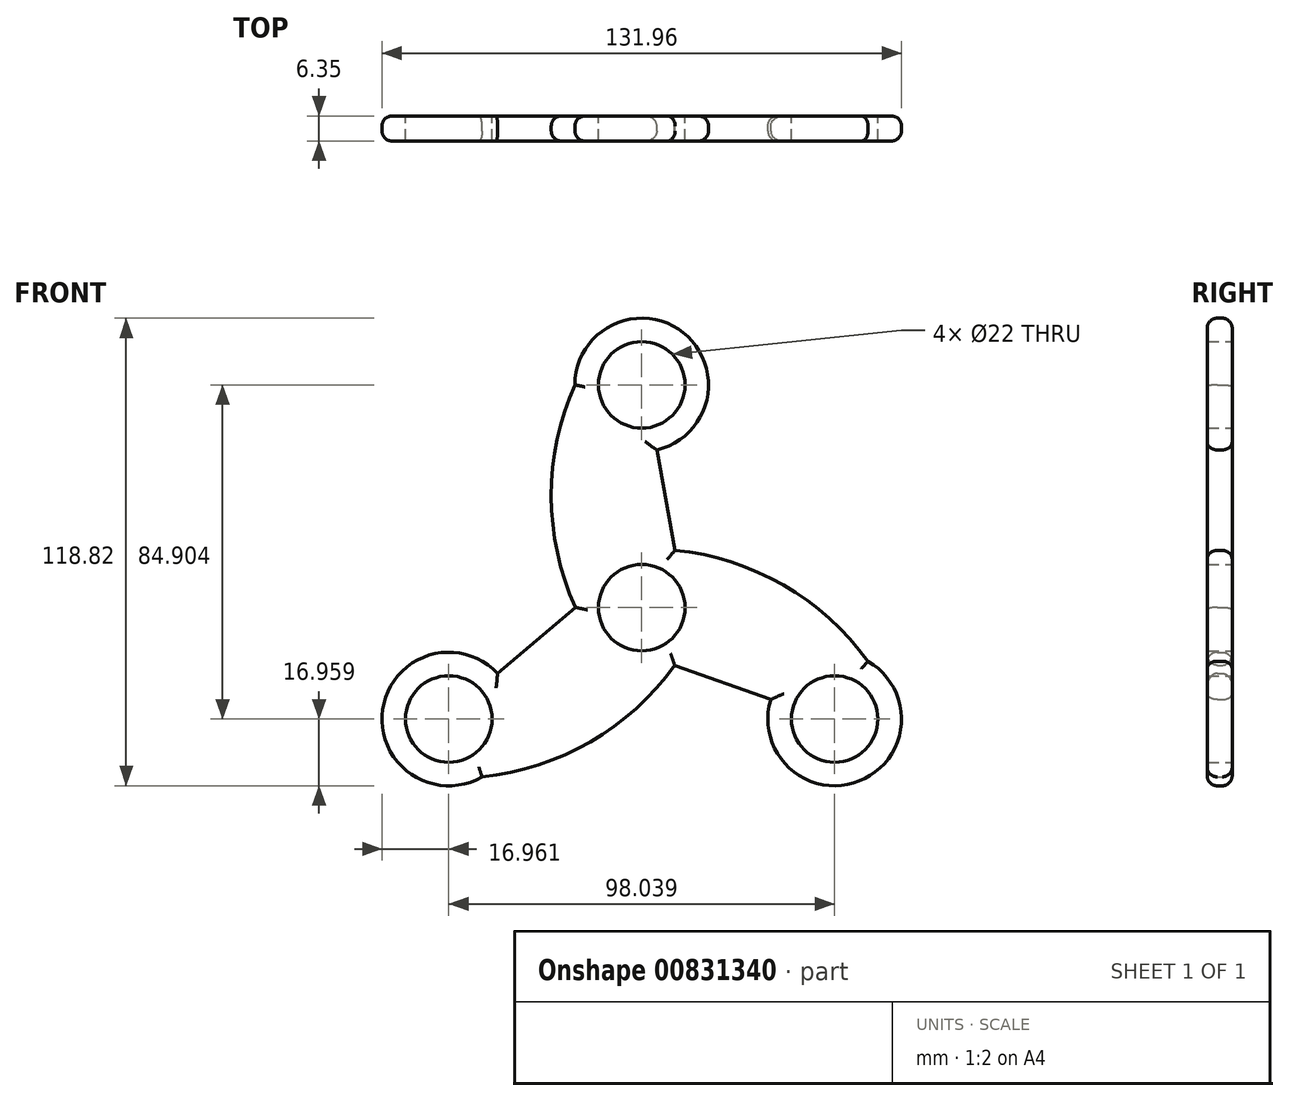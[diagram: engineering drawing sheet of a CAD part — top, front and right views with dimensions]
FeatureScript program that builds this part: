
annotation { "Feature Type Name" : "Feature", "Feature Type Description" : "" }
export const myFeature = defineFeature(function(context is Context, id is Id, definition is map)
    precondition{}
    {
        {
            var Q0;
            Q0=qCreatedBy(makeId("Front.planeOp"),FACE);
            var sketch = newSketch(context, id + "F0", { "sketchPlane" : qUnion([Q0])});
            skCircle(sketch, "E0", {"center": v(0, 0) * mm, "radius": 11 * mm});
            skCircle(sketch, "E1", {"center": v(0, 56.6) * mm, "radius": 11 * mm});
            skArc(sketch, "E2", {"start": v(3.84, 40.08) * mm, "mid": v(10.55, 69.89) * mm, "end": v(-16.96, 56.6) * mm});
            skArc(sketch, "E3", {"start": v(-16.82, 0.13) * mm, "mid": v(-16.82, 0.07) * mm, "end": v(-16.83, 0) * mm});
            skArc(sketch, "E4", {"start": v(-16.96, 56.6) * mm, "mid": v(-22.98, 28.29) * mm, "end": v(-16.83, 0) * mm});
            skLineSegment(sketch, "E5", {"start": v(3.84, 40.08) * mm, "end": v(8.53, 14.5) * mm});
            skCircle(sketch, "E6.1.0", {"center": v(-49.02, -28.3) * mm, "radius": 11 * mm});
            skArc(sketch, "E6.1.1", {"start": v(-36.64, -16.71) * mm, "mid": v(-65.8, -25.8) * mm, "end": v(-40.54, -42.99) * mm});
            skLineSegment(sketch, "E6.1.2", {"start": v(-36.64, -16.71) * mm, "end": v(-16.82, 0.13) * mm});
            skArc(sketch, "E6.1.3", {"start": v(-40.54, -42.99) * mm, "mid": v(-13, -34.04) * mm, "end": v(8.41, -14.57) * mm});
            skCircle(sketch, "E6.2.0", {"center": v(49.02, -28.3) * mm, "radius": 11 * mm});
            skArc(sketch, "E6.2.1", {"start": v(32.8, -23.37) * mm, "mid": v(55.25, -44.08) * mm, "end": v(57.5, -13.61) * mm});
            skLineSegment(sketch, "E6.2.2", {"start": v(32.8, -23.37) * mm, "end": v(8.3, -14.64) * mm});
            skArc(sketch, "E6.2.3", {"start": v(57.5, -13.61) * mm, "mid": v(35.99, 5.76) * mm, "end": v(8.41, 14.57) * mm});
            skArc(sketch, "E7.trimOffspring", {"start": v(8.53, 14.5) * mm, "mid": v(8.47, 14.54) * mm, "end": v(8.41, 14.57) * mm});
            skArc(sketch, "E8.trimOffspring", {"start": v(8.3, -14.64) * mm, "mid": v(8.36, -14.6) * mm, "end": v(8.41, -14.57) * mm});
            skSolve(sketch);
        }
        {
            var Q0;
            Q0 = qSketchRegion(id + "F0", true);
            extrude(context, id + "F1", {"entities" : qUnion([Q0]), "depth" : 6.35 * mm, "offsetDistance" : 25.4 * mm});
        }
        {
            var Q0;
            Q0=makeQuery(id+"F1.opExtrude","CAP_EDGE",EDGE,{"disambiguationData":[OSD([sQuery(id+"F0.wireOp",EDGE,"E2")])],"isStart":false});
            var Q1;
            Q1=makeQuery(id+"F1.opExtrude","CAP_EDGE",EDGE,{"disambiguationData":[OSD([sQuery(id+"F0.wireOp",EDGE,"E5")])],"isStart":false});
            var Q2;
            Q2=makeQuery(id+"F1.opExtrude","CAP_EDGE",EDGE,{"disambiguationData":[OSD([sQuery(id+"F0.wireOp",EDGE,"E4")])],"isStart":false});
            var Q3;
            Q3=makeQuery(id+"F1.opExtrude","CAP_EDGE",EDGE,{"disambiguationData":[OSD([sQuery(id+"F0.wireOp",EDGE,"E6.2.3")])],"isStart":false});
            var Q4;
            Q4=makeQuery(id+"F1.opExtrude","CAP_EDGE",EDGE,{"disambiguationData":[OSD([sQuery(id+"F0.wireOp",EDGE,"E6.2.1")])],"isStart":false});
            var Q5;
            Q5=makeQuery(id+"F1.opExtrude","CAP_EDGE",EDGE,{"disambiguationData":[OSD([sQuery(id+"F0.wireOp",EDGE,"E6.2.2")])],"isStart":false});
            var Q6;
            Q6=makeQuery(id+"F1.opExtrude","CAP_EDGE",EDGE,{"disambiguationData":[OSD([sQuery(id+"F0.wireOp",EDGE,"E6.1.3")])],"isStart":false});
            var Q7;
            Q7=makeQuery(id+"F1.opExtrude","CAP_EDGE",EDGE,{"disambiguationData":[OSD([sQuery(id+"F0.wireOp",EDGE,"E6.1.2")])],"isStart":false});
            var Q8;
            Q8=makeQuery(id+"F1.opExtrude","CAP_EDGE",EDGE,{"disambiguationData":[OSD([sQuery(id+"F0.wireOp",EDGE,"E6.1.1")])],"isStart":false});
            fillet(context, id + "F2", {"entities" : qUnion([Q0, Q1, Q2, Q3, Q4, Q5, Q6, Q7, Q8]), "radius" : 2.54 * mm, "tangentPropagation" : true, "allowEdgeOverflow" : false});
        }
        {
            var Q0;
            Q0=makeQuery(id+"F1.opExtrude","CAP_EDGE",EDGE,{"disambiguationData":[OSD([sQuery(id+"F0.wireOp",EDGE,"E2")])],"isStart":true});
            var Q1;
            Q1=makeQuery(id+"F1.opExtrude","CAP_EDGE",EDGE,{"disambiguationData":[OSD([sQuery(id+"F0.wireOp",EDGE,"E4")])],"isStart":true});
            var Q2;
            Q2=makeQuery(id+"F1.opExtrude","CAP_EDGE",EDGE,{"disambiguationData":[OSD([sQuery(id+"F0.wireOp",EDGE,"E6.1.2")])],"isStart":true});
            var Q3;
            Q3=makeQuery(id+"F1.opExtrude","CAP_EDGE",EDGE,{"disambiguationData":[OSD([sQuery(id+"F0.wireOp",EDGE,"E6.1.1")])],"isStart":true});
            var Q4;
            Q4=makeQuery(id+"F1.opExtrude","CAP_EDGE",EDGE,{"disambiguationData":[OSD([sQuery(id+"F0.wireOp",EDGE,"E6.1.3")])],"isStart":true});
            var Q5;
            Q5=makeQuery(id+"F1.opExtrude","CAP_EDGE",EDGE,{"disambiguationData":[OSD([sQuery(id+"F0.wireOp",EDGE,"E6.2.2")])],"isStart":true});
            var Q6;
            Q6=makeQuery(id+"F1.opExtrude","CAP_EDGE",EDGE,{"disambiguationData":[OSD([sQuery(id+"F0.wireOp",EDGE,"E6.2.1")])],"isStart":true});
            var Q7;
            Q7=makeQuery(id+"F1.opExtrude","CAP_EDGE",EDGE,{"disambiguationData":[OSD([sQuery(id+"F0.wireOp",EDGE,"E6.2.3")])],"isStart":true});
            var Q8;
            Q8=makeQuery(id+"F1.opExtrude","CAP_EDGE",EDGE,{"disambiguationData":[OSD([sQuery(id+"F0.wireOp",EDGE,"E5")])],"isStart":true});
            fillet(context, id + "F3", {"entities" : qUnion([Q0, Q1, Q2, Q3, Q4, Q5, Q6, Q7, Q8]), "radius" : 2.54 * mm, "tangentPropagation" : true, "allowEdgeOverflow" : false});
        }
    });
